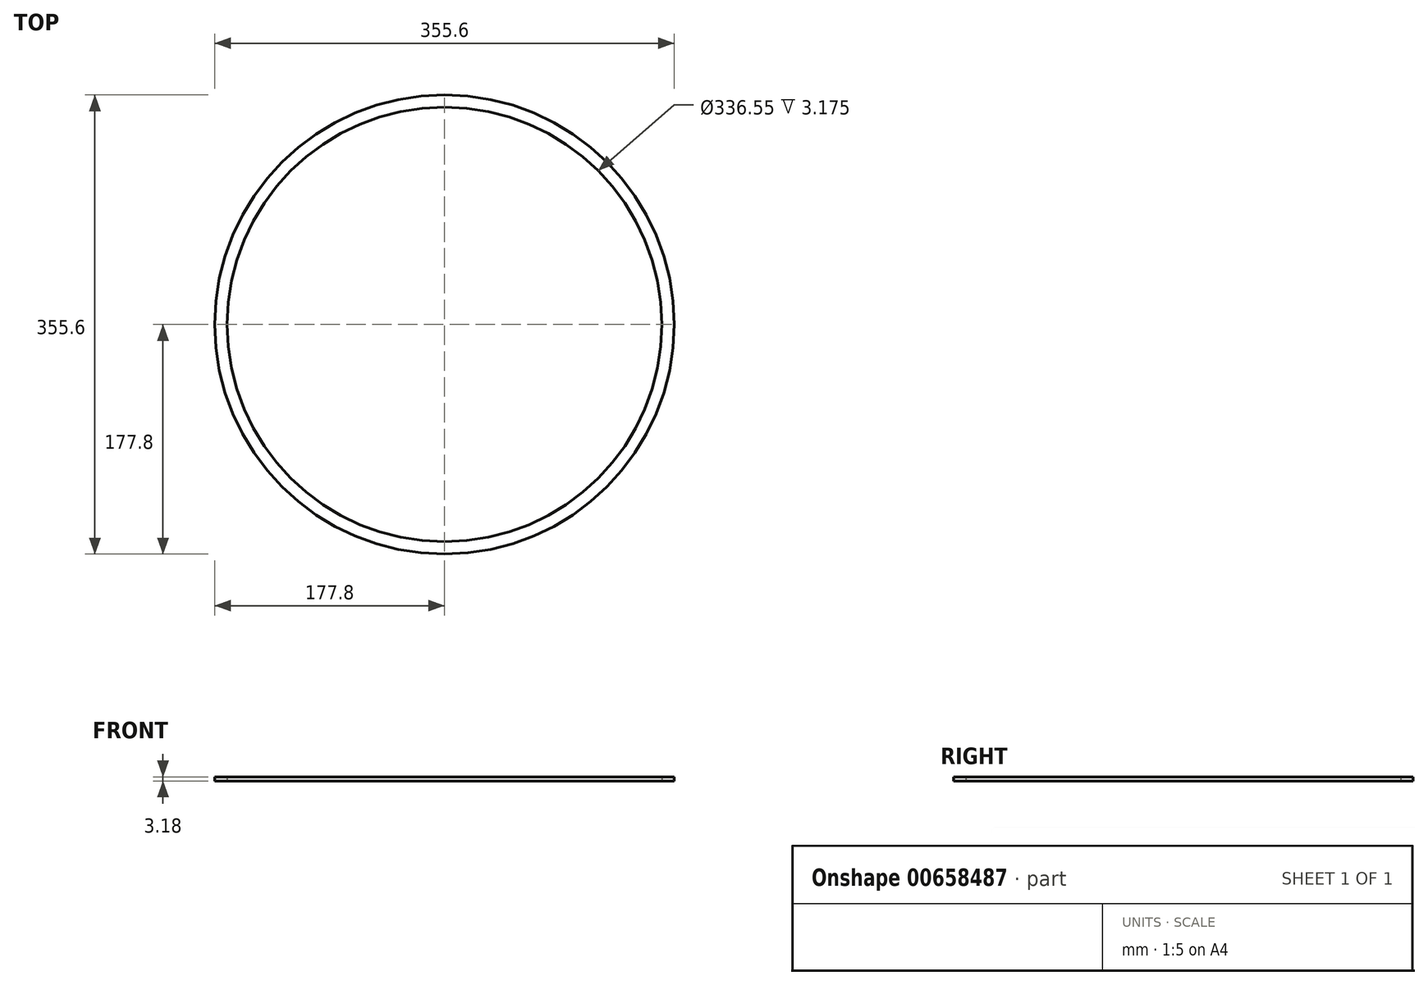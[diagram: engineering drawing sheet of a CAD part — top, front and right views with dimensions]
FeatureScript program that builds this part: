
annotation { "Feature Type Name" : "Feature", "Feature Type Description" : "" }
export const myFeature = defineFeature(function(context is Context, id is Id, definition is map)
    precondition{}
    {
        {
            var Q0;
            Q0=qCreatedBy(makeId("Top.planeOp"),FACE);
            var sketch = newSketch(context, id + "F0", { "sketchPlane" : qUnion([Q0])});
            skCircle(sketch, "E0", {"center": v(0, 0) * mm, "radius": 177.8 * mm});
            skCircle(sketch, "E1", {"center": v(0, 0) * mm, "radius": 168.28 * mm});
            skSolve(sketch);
        }
        {
            var Q0;
            Q0=makeQuery(id+"F0.imprint","IMPRINT",FACE,{"disambiguationData":[TD([[makeQuery(id+"F0.imprint","IMPRINT",EDGE,{"derivedFrom":sQuery(id+"F0.wireOp",EDGE,"E0")}),1.0]])]});
            extrude(context, id + "F1", {"entities" : qUnion([Q0]), "depth" : 3.17 * mm, "offsetDistance" : 25.4 * mm});
        }
    });
